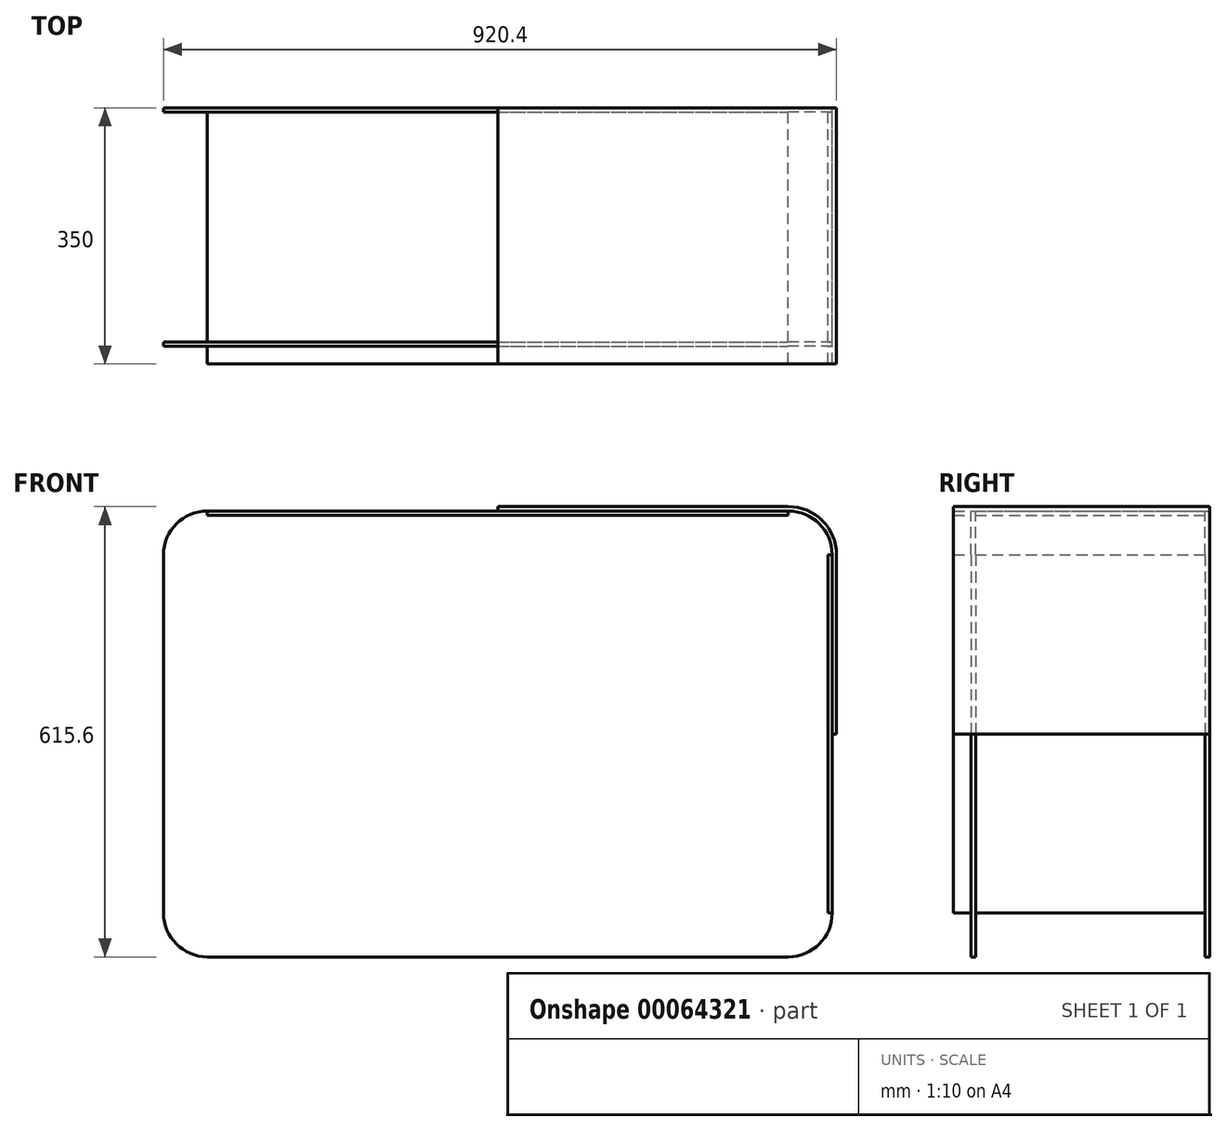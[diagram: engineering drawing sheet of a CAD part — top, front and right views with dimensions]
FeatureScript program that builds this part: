
annotation { "Feature Type Name" : "Feature", "Feature Type Description" : "" }
export const myFeature = defineFeature(function(context is Context, id is Id, definition is map)
    precondition{}
    {
        {
            var Q0;
            Q0=qCreatedBy(makeId("Front.planeOp"),FACE);
            var sketch = newSketch(context, id + "F0", { "sketchPlane" : qUnion([Q0])});
            skLineSegment(sketch, "E0.rect.bottom", {"start": v(397.2, 304.8) * mm, "end": v(0, 304.8) * mm});
            skLineSegment(sketch, "E0.rect.left", {"start": v(457.2, 244.8) * mm, "end": v(457.2, 0) * mm});
            skPoint(sketch, "E0.rect.middle", {"position": v(0, 0) * mm});
            skPoint(sketch, "E1.visualSharp", {"position": v(-457.2, 304.8) * mm});
            skPoint(sketch, "E2.visualSharp", {"position": v(457.2, 304.8) * mm});
            skArc(sketch, "E2.filletArc", {"start": v(457.2, 244.8) * mm, "mid": v(439.63, 287.23) * mm, "end": v(397.2, 304.8) * mm});
            skPoint(sketch, "E3.visualSharp", {"position": v(-457.2, -304.8) * mm});
            skPoint(sketch, "E4.visualSharp", {"position": v(457.2, -304.8) * mm});
            skLineSegment(sketch, "E5", {"start": v(0, 0) * mm, "end": v(0, 526.98) * mm});
            skLineSegment(sketch, "E6", {"start": v(667.96, 0) * mm, "end": v(0, 0) * mm});
            skLineSegment(sketch, "E7.0", {"start": v(397.2, 310.8) * mm, "end": v(0, 310.8) * mm});
            skArc(sketch, "E7.1", {"start": v(463.2, 244.8) * mm, "mid": v(443.87, 291.47) * mm, "end": v(397.2, 310.8) * mm});
            skLineSegment(sketch, "E7.2", {"start": v(463.2, 244.8) * mm, "end": v(463.2, 0) * mm});
            skLineSegment(sketch, "E8.0", {"start": v(397.2, 298.8) * mm, "end": v(0, 298.8) * mm});
            skLineSegment(sketch, "E9.0", {"start": v(451.2, 244.8) * mm, "end": v(451.2, 0) * mm});
            skLineSegment(sketch, "E10.MirrorCS", {"start": v(397.2, -304.8) * mm, "end": v(0, -304.8) * mm});
            skLineSegment(sketch, "E11.MirrorCS", {"start": v(457.2, -244.8) * mm, "end": v(457.2, 0) * mm});
            skLineSegment(sketch, "E12.MirrorCS", {"start": v(397.2, -310.8) * mm, "end": v(0, -310.8) * mm});
            skLineSegment(sketch, "E13.MirrorCS", {"start": v(451.2, -244.8) * mm, "end": v(451.2, 0) * mm});
            skArc(sketch, "E14.MirrorCS", {"start": v(457.2, -244.8) * mm, "mid": v(439.63, -287.23) * mm, "end": v(397.2, -304.8) * mm});
            skArc(sketch, "E15.MirrorCS", {"start": v(463.2, -244.8) * mm, "mid": v(443.87, -291.47) * mm, "end": v(397.2, -310.8) * mm});
            skLineSegment(sketch, "E16.MirrorCS", {"start": v(397.2, -298.8) * mm, "end": v(0, -298.8) * mm});
            skLineSegment(sketch, "E17.MirrorCS", {"start": v(463.2, -244.8) * mm, "end": v(463.2, 0) * mm});
            skLineSegment(sketch, "E18.bottom", {"start": v(1425.63, 785.2) * mm, "end": v(3864.03, 785.2) * mm});
            skLineSegment(sketch, "E18.top", {"start": v(1425.63, -434) * mm, "end": v(3864.03, -434) * mm});
            skLineSegment(sketch, "E18.left", {"start": v(1425.63, 785.2) * mm, "end": v(1425.63, -434) * mm});
            skLineSegment(sketch, "E18.right", {"start": v(3864.03, 785.2) * mm, "end": v(3864.03, -434) * mm});
            skLineSegment(sketch, "E19.bottom", {"start": v(1421.93, -434) * mm, "end": v(2621.93, -434) * mm});
            skLineSegment(sketch, "E19.top", {"start": v(1421.93, 366) * mm, "end": v(2621.93, 366) * mm});
            skLineSegment(sketch, "E19.left", {"start": v(1421.93, -434) * mm, "end": v(1421.93, 366) * mm});
            skLineSegment(sketch, "E19.right", {"start": v(2621.93, -434) * mm, "end": v(2621.93, 366) * mm});
            skLineSegment(sketch, "E20", {"start": v(2644.83, -434) * mm, "end": v(2644.83, 785.2) * mm});
            skArc(sketch, "E21.MirrorCS", {"start": v(-463.2, -244.8) * mm, "mid": v(-443.87, -291.47) * mm, "end": v(-397.2, -310.8) * mm});
            skArc(sketch, "E22.MirrorCS", {"start": v(-457.2, -244.8) * mm, "mid": v(-439.63, -287.23) * mm, "end": v(-397.2, -304.8) * mm});
            skLineSegment(sketch, "E23.MirrorCS", {"start": v(-397.2, 304.8) * mm, "end": v(0, 304.8) * mm});
            skLineSegment(sketch, "E24.MirrorCS", {"start": v(-397.2, -304.8) * mm, "end": v(0, -304.8) * mm});
            skArc(sketch, "E25.MirrorCS", {"start": v(-463.2, 244.8) * mm, "mid": v(-443.87, 291.47) * mm, "end": v(-397.2, 310.8) * mm});
            skArc(sketch, "E26.MirrorCS", {"start": v(-457.2, 244.8) * mm, "mid": v(-439.63, 287.23) * mm, "end": v(-397.2, 304.8) * mm});
            skLineSegment(sketch, "E27.MirrorCS", {"start": v(-457.2, 244.8) * mm, "end": v(-457.2, 0) * mm});
            skLineSegment(sketch, "E28.MirrorCS", {"start": v(-397.2, -298.8) * mm, "end": v(0, -298.8) * mm});
            skLineSegment(sketch, "E29.MirrorCS", {"start": v(-397.2, -310.8) * mm, "end": v(0, -310.8) * mm});
            skLineSegment(sketch, "E30.MirrorCS", {"start": v(-457.2, -244.8) * mm, "end": v(-457.2, 0) * mm});
            skLineSegment(sketch, "E31.MirrorCS", {"start": v(-451.2, 244.8) * mm, "end": v(-451.2, 0) * mm});
            skLineSegment(sketch, "E32.MirrorCS", {"start": v(-397.2, 298.8) * mm, "end": v(0, 298.8) * mm});
            skLineSegment(sketch, "E33.MirrorCS", {"start": v(-463.2, 244.8) * mm, "end": v(-463.2, 0) * mm});
            skLineSegment(sketch, "E34.MirrorCS", {"start": v(-463.2, -244.8) * mm, "end": v(-463.2, 0) * mm});
            skLineSegment(sketch, "E35.MirrorCS", {"start": v(-397.2, 310.8) * mm, "end": v(0, 310.8) * mm});
            skLineSegment(sketch, "E36.MirrorCS", {"start": v(-667.96, 0) * mm, "end": v(0, 0) * mm, "construction": true});
            skLineSegment(sketch, "E37.MirrorCS", {"start": v(-451.2, -244.8) * mm, "end": v(-451.2, 0) * mm});
            skLineSegment(sketch, "E38", {"start": v(397.2, 298.8) * mm, "end": v(397.2, 304.8) * mm});
            skLineSegment(sketch, "E39", {"start": v(451.2, 244.8) * mm, "end": v(457.2, 244.8) * mm});
            skLineSegment(sketch, "E40.MirrorCS", {"start": v(397.2, -298.8) * mm, "end": v(397.2, -304.8) * mm});
            skLineSegment(sketch, "E41.MirrorCS", {"start": v(451.2, -244.8) * mm, "end": v(457.2, -244.8) * mm});
            skLineSegment(sketch, "E42.MirrorCS", {"start": v(-397.2, 298.8) * mm, "end": v(-397.2, 304.8) * mm});
            skLineSegment(sketch, "E43.MirrorCS", {"start": v(-451.2, 244.8) * mm, "end": v(-457.2, 244.8) * mm});
            skLineSegment(sketch, "E44.MirrorCS", {"start": v(-451.2, -244.8) * mm, "end": v(-457.2, -244.8) * mm});
            skLineSegment(sketch, "E45.MirrorCS", {"start": v(-397.2, -298.8) * mm, "end": v(-397.2, -304.8) * mm});
            skLineSegment(sketch, "E46.bottom", {"start": v(1396.97, -1773.98) * mm, "end": v(1746.97, -1773.98) * mm});
            skLineSegment(sketch, "E46.top", {"start": v(1396.97, -2518.98) * mm, "end": v(1746.97, -2518.98) * mm});
            skLineSegment(sketch, "E46.left", {"start": v(1396.97, -1773.98) * mm, "end": v(1396.97, -2518.98) * mm});
            skLineSegment(sketch, "E46.right", {"start": v(1746.97, -1773.98) * mm, "end": v(1746.97, -2518.98) * mm});
            skLineSegment(sketch, "E47.1.0.0", {"start": v(1746.97, -2518.98) * mm, "end": v(2096.97, -2518.98) * mm});
            skLineSegment(sketch, "E47.1.0.1", {"start": v(2096.97, -1773.98) * mm, "end": v(2096.97, -2518.98) * mm});
            skLineSegment(sketch, "E47.1.0.2", {"start": v(1746.97, -1773.98) * mm, "end": v(2096.97, -1773.98) * mm});
            skLineSegment(sketch, "E47.2.0.0", {"start": v(2096.97, -2518.98) * mm, "end": v(2446.97, -2518.98) * mm});
            skLineSegment(sketch, "E47.2.0.1", {"start": v(2446.97, -1773.98) * mm, "end": v(2446.97, -2518.98) * mm});
            skLineSegment(sketch, "E47.2.0.2", {"start": v(2096.97, -1773.98) * mm, "end": v(2446.97, -1773.98) * mm});
            skLineSegment(sketch, "E47.direction1", {"start": v(1396.97, -2518.98) * mm, "end": v(1746.97, -2518.98) * mm, "construction": true});
            skLineSegment(sketch, "E48.bottom", {"start": v(2698.8, -1773.27) * mm, "end": v(3048.8, -1773.27) * mm});
            skLineSegment(sketch, "E48.top", {"start": v(2698.8, -2518.27) * mm, "end": v(3048.8, -2518.27) * mm});
            skLineSegment(sketch, "E48.left", {"start": v(2698.8, -1773.27) * mm, "end": v(2698.8, -2518.27) * mm});
            skLineSegment(sketch, "E48.right", {"start": v(3048.8, -1773.27) * mm, "end": v(3048.8, -2518.27) * mm});
            skLineSegment(sketch, "E49.bottom", {"start": v(1430.76, -3016.82) * mm, "end": v(2225.76, -3016.82) * mm});
            skLineSegment(sketch, "E49.top", {"start": v(1430.76, -3316.82) * mm, "end": v(2225.76, -3316.82) * mm});
            skLineSegment(sketch, "E49.left", {"start": v(1430.76, -3016.82) * mm, "end": v(1430.76, -3316.82) * mm});
            skLineSegment(sketch, "E49.right", {"start": v(2225.76, -3016.82) * mm, "end": v(2225.76, -3316.82) * mm});
            skLineSegment(sketch, "E50.bottom", {"start": v(4728.96, 341) * mm, "end": v(5643.36, 341) * mm});
            skLineSegment(sketch, "E50.top", {"start": v(4728.96, -268.6) * mm, "end": v(5643.36, -268.6) * mm});
            skLineSegment(sketch, "E50.left", {"start": v(4728.96, 341) * mm, "end": v(4728.96, -268.6) * mm});
            skLineSegment(sketch, "E50.right", {"start": v(5643.36, 341) * mm, "end": v(5643.36, -268.6) * mm});
            skLineSegment(sketch, "E51.bottom", {"start": v(3200.39, -380.36) * mm, "end": v(3809.99, -380.36) * mm});
            skLineSegment(sketch, "E51.top", {"start": v(3200.39, 534.04) * mm, "end": v(3809.99, 534.04) * mm});
            skLineSegment(sketch, "E51.left", {"start": v(3200.39, -380.36) * mm, "end": v(3200.39, 534.04) * mm});
            skLineSegment(sketch, "E51.right", {"start": v(3809.99, -380.36) * mm, "end": v(3809.99, 534.04) * mm});
            skLineSegment(sketch, "E52.bottom", {"start": v(3993.98, -1809.5) * mm, "end": v(6433.98, -1809.5) * mm});
            skLineSegment(sketch, "E52.top", {"start": v(3993.98, -3029.5) * mm, "end": v(6433.98, -3029.5) * mm});
            skLineSegment(sketch, "E52.left", {"start": v(3993.98, -1809.5) * mm, "end": v(3993.98, -3029.5) * mm});
            skLineSegment(sketch, "E52.right", {"start": v(6433.98, -1809.5) * mm, "end": v(6433.98, -3029.5) * mm});
            skLineSegment(sketch, "E53", {"start": v(5213.98, -1809.5) * mm, "end": v(5213.98, -3029.5) * mm});
            skLineSegment(sketch, "E54", {"start": v(3993.98, -2229.5) * mm, "end": v(5213.98, -2229.5) * mm});
            skLineSegment(sketch, "E55", {"start": v(5773.98, -1809.5) * mm, "end": v(5773.98, -3029.5) * mm});
            skSolve(sketch);
        }
        {
            var Q0;
            {var subQ1=sQuery(id+"F0.wireOp",EDGE,"E0.rect.bottom");Q0=makeQuery(id+"F0.imprint","IMPRINT",FACE,{"disambiguationData":[TD([[makeQuery(id+"F0.imprint","IMPRINT",EDGE,{"derivedFrom":subQ1}),-1.0]])]});}
            extrude(context, id + "F1", {"entities" : qUnion([Q0]), "depth" : 350 * mm});
        }
        {
            var Q0;
            {var subQ0=sQuery(id+"F0.wireOp",EDGE,"E23.MirrorCS");Q0=makeQuery(id+"F0.imprint","IMPRINT",FACE,{"disambiguationData":[TD([[makeQuery(id+"F0.imprint","IMPRINT",EDGE,{"derivedFrom":subQ0}),-1.0]])]});}
            var Q1;
            {var subQ0=sQuery(id+"F0.wireOp",EDGE,"E0.rect.bottom");Q1=makeQuery(id+"F0.imprint","IMPRINT",FACE,{"disambiguationData":[TD([[makeQuery(id+"F0.imprint","IMPRINT",EDGE,{"derivedFrom":subQ0}),1.0]])]});}
            var Q2;
            {var subQ0=sQuery(id+"F0.wireOp",EDGE,"E0.rect.left");Q2=makeQuery(id+"F0.imprint","IMPRINT",FACE,{"disambiguationData":[TD([[makeQuery(id+"F0.imprint","IMPRINT",EDGE,{"derivedFrom":subQ0}),-1.0]])]});}
            var Q3;
            {var subQ0=sQuery(id+"F0.wireOp",EDGE,"E11.MirrorCS");Q3=makeQuery(id+"F0.imprint","IMPRINT",FACE,{"disambiguationData":[TD([[makeQuery(id+"F0.imprint","IMPRINT",EDGE,{"derivedFrom":subQ0}),1.0]])]});}
            extrude(context, id + "F2", {"entities" : qUnion([Q0, Q1, Q2, Q3]), "depth" : 314 * mm});
        }
        {
            var Q0;
            Q0=makeQuery(id+"F2.opExtrude","SWEPT_BODY",BODY,{"disambiguationData":[OSD([sQuery(id+"F0.wireOp",EDGE,"E0.rect.bottom"),sQuery(id+"F0.wireOp",EDGE,"E8.0"),sQuery(id+"F0.wireOp",EDGE,"E23.MirrorCS"),sQuery(id+"F0.wireOp",EDGE,"E32.MirrorCS"),sQuery(id+"F0.wireOp",EDGE,"E38"),sQuery(id+"F0.wireOp",EDGE,"E42.MirrorCS")])]});
            var Q1;
            Q1=makeQuery(id+"F2.opExtrude","SWEPT_BODY",BODY,{"disambiguationData":[OSD([sQuery(id+"F0.wireOp",EDGE,"E0.rect.left"),sQuery(id+"F0.wireOp",EDGE,"E9.0"),sQuery(id+"F0.wireOp",EDGE,"E11.MirrorCS"),sQuery(id+"F0.wireOp",EDGE,"E13.MirrorCS"),sQuery(id+"F0.wireOp",EDGE,"E39"),sQuery(id+"F0.wireOp",EDGE,"E41.MirrorCS")])]});
            var Q2;
            Q2=makeQuery(id+"F2.opExtrude","SWEPT_EDGE",EDGE,{"disambiguationData":[OSD([sQuery(id+"F0.wireOp",EDGE,"E32.MirrorCS"),sQuery(id+"F0.wireOp",EDGE,"E42.MirrorCS")])]});
            transform(context, id + "F3", {"entities" : qUnion([Q0, Q1]), "transformType" : TransformType.TRANSLATION_DISTANCE, "transformDirection" : qUnion([Q2]), "distance" : 6 * mm, "oppositeDirection" : true, "makeCopy" : false});
        }
        {
            var Q0;
            {var subQ0=sQuery(id+"F0.wireOp",EDGE,"E0.rect.bottom");Q0=makeQuery(id+"F0.imprint","IMPRINT",FACE,{"disambiguationData":[TD([[makeQuery(id+"F0.imprint","IMPRINT",EDGE,{"derivedFrom":subQ0}),1.0]])]});}
            var Q1;
            {var subQ0=sQuery(id+"F0.wireOp",EDGE,"E0.rect.left");Q1=makeQuery(id+"F0.imprint","IMPRINT",FACE,{"disambiguationData":[TD([[makeQuery(id+"F0.imprint","IMPRINT",EDGE,{"derivedFrom":subQ0}),-1.0]])]});}
            var Q2;
            {var subQ0=sQuery(id+"F0.wireOp",EDGE,"E23.MirrorCS");Q2=makeQuery(id+"F0.imprint","IMPRINT",FACE,{"disambiguationData":[TD([[makeQuery(id+"F0.imprint","IMPRINT",EDGE,{"derivedFrom":subQ0}),-1.0]])]});}
            var Q3;
            {var subQ0=sQuery(id+"F0.wireOp",EDGE,"E11.MirrorCS");Q3=makeQuery(id+"F0.imprint","IMPRINT",FACE,{"disambiguationData":[TD([[makeQuery(id+"F0.imprint","IMPRINT",EDGE,{"derivedFrom":subQ0}),1.0]])]});}
            extrude(context, id + "F4", {"entities" : qUnion([Q0, Q1, Q2, Q3]), "depth" : 24 * mm});
        }
        {
            var Q0;
            Q0=makeQuery(id+"F4.opExtrude","SWEPT_BODY",BODY,{"disambiguationData":[OSD([sQuery(id+"F0.wireOp",EDGE,"E0.rect.left"),sQuery(id+"F0.wireOp",EDGE,"E9.0"),sQuery(id+"F0.wireOp",EDGE,"E11.MirrorCS"),sQuery(id+"F0.wireOp",EDGE,"E13.MirrorCS"),sQuery(id+"F0.wireOp",EDGE,"E39"),sQuery(id+"F0.wireOp",EDGE,"E41.MirrorCS")])]});
            var Q1;
            Q1=makeQuery(id+"F4.opExtrude","SWEPT_BODY",BODY,{"disambiguationData":[OSD([sQuery(id+"F0.wireOp",EDGE,"E0.rect.bottom"),sQuery(id+"F0.wireOp",EDGE,"E8.0"),sQuery(id+"F0.wireOp",EDGE,"E23.MirrorCS"),sQuery(id+"F0.wireOp",EDGE,"E32.MirrorCS"),sQuery(id+"F0.wireOp",EDGE,"E38"),sQuery(id+"F0.wireOp",EDGE,"E42.MirrorCS")])]});
            var Q2;
            Q2=makeQuery(id+"F2.opExtrude","SWEPT_EDGE",EDGE,{"disambiguationData":[OSD([sQuery(id+"F0.wireOp",EDGE,"E8.0"),sQuery(id+"F0.wireOp",EDGE,"E38")])]});
            transform(context, id + "F5", {"entities" : qUnion([Q0, Q1]), "transformType" : TransformType.TRANSLATION_DISTANCE, "transformDirection" : qUnion([Q2]), "distance" : 326 * mm, "oppositeDirection" : true, "makeCopy" : false});
        }
        {
            var Q0;
            {var subQ0=sQuery(id+"F0.wireOp",EDGE,"E0.rect.left");Q0=makeQuery(id+"F0.imprint","IMPRINT",FACE,{"disambiguationData":[TD([[makeQuery(id+"F0.imprint","IMPRINT",EDGE,{"derivedFrom":subQ0}),-1.0]])]});}
            var Q1;
            Q1=makeQuery(id+"F0.imprint","IMPRINT",FACE,{"disambiguationData":[TD([[makeQuery(id+"F0.imprint","IMPRINT",EDGE,{"derivedFrom":sQuery(id+"F0.wireOp",EDGE,"E2.filletArc")}),1.0]])]});
            var Q2;
            {var subQ0=sQuery(id+"F0.wireOp",EDGE,"E11.MirrorCS");Q2=makeQuery(id+"F0.imprint","IMPRINT",FACE,{"disambiguationData":[TD([[makeQuery(id+"F0.imprint","IMPRINT",EDGE,{"derivedFrom":subQ0}),1.0]])]});}
            var Q3;
            {var subQ4=sQuery(id+"F0.wireOp",EDGE,"E13.MirrorCS");Q3=makeQuery(id+"F0.imprint","IMPRINT",FACE,{"disambiguationData":[TD([[makeQuery(id+"F0.imprint","IMPRINT",EDGE,{"derivedFrom":subQ4}),1.0]])]});}
            var Q4;
            Q4=makeQuery(id+"F0.imprint","IMPRINT",FACE,{"disambiguationData":[TD([[makeQuery(id+"F0.imprint","IMPRINT",EDGE,{"derivedFrom":sQuery(id+"F0.wireOp",EDGE,"E27.MirrorCS")}),1.0]])]});
            var Q5;
            Q5=makeQuery(id+"F0.imprint","IMPRINT",FACE,{"disambiguationData":[TD([[makeQuery(id+"F0.imprint","IMPRINT",EDGE,{"derivedFrom":sQuery(id+"F0.wireOp",EDGE,"E10.MirrorCS")}),-1.0]])]});
            var Q6;
            {var subQ0=sQuery(id+"F0.wireOp",EDGE,"E23.MirrorCS");Q6=makeQuery(id+"F0.imprint","IMPRINT",FACE,{"disambiguationData":[TD([[makeQuery(id+"F0.imprint","IMPRINT",EDGE,{"derivedFrom":subQ0}),-1.0]])]});}
            var Q7;
            {var subQ0=sQuery(id+"F0.wireOp",EDGE,"E0.rect.bottom");Q7=makeQuery(id+"F0.imprint","IMPRINT",FACE,{"disambiguationData":[TD([[makeQuery(id+"F0.imprint","IMPRINT",EDGE,{"derivedFrom":subQ0}),1.0]])]});}
            extrude(context, id + "F6", {"entities" : qUnion([Q0, Q1, Q2, Q3, Q4, Q5, Q6, Q7]), "depth" : 6 * mm});
        }
        {
            var Q0;
            Q0=makeQuery(id+"F6.opExtrude","SWEPT_BODY",BODY,{"disambiguationData":[OSD([sQuery(id+"F0.wireOp",EDGE,"E0.rect.bottom"),sQuery(id+"F0.wireOp",EDGE,"E0.rect.left"),sQuery(id+"F0.wireOp",EDGE,"E2.filletArc"),sQuery(id+"F0.wireOp",EDGE,"E10.MirrorCS"),sQuery(id+"F0.wireOp",EDGE,"E11.MirrorCS"),sQuery(id+"F0.wireOp",EDGE,"E14.MirrorCS"),sQuery(id+"F0.wireOp",EDGE,"E22.MirrorCS"),sQuery(id+"F0.wireOp",EDGE,"E23.MirrorCS"),sQuery(id+"F0.wireOp",EDGE,"E24.MirrorCS"),sQuery(id+"F0.wireOp",EDGE,"E26.MirrorCS"),sQuery(id+"F0.wireOp",EDGE,"E27.MirrorCS"),sQuery(id+"F0.wireOp",EDGE,"E30.MirrorCS")])]});
            var Q1;
            Q1=makeQuery(id+"F2.opExtrude","SWEPT_EDGE",EDGE,{"disambiguationData":[OSD([sQuery(id+"F0.wireOp",EDGE,"E13.MirrorCS"),sQuery(id+"F0.wireOp",EDGE,"E41.MirrorCS")])]});
            var Q2;
            Q2=makeQuery(id+"F2.opExtrude","SWEPT_EDGE",EDGE,{"disambiguationData":[OSD([sQuery(id+"F0.wireOp",EDGE,"E11.MirrorCS"),sQuery(id+"F0.wireOp",EDGE,"E14.MirrorCS"),sQuery(id+"F0.wireOp",EDGE,"E41.MirrorCS")])]});
            transform(context, id + "F7", {"entities" : qUnion([Q0]), "transformType" : TransformType.TRANSLATION_DISTANCE, "transformDirection" : qUnion([Q2]), "distance" : 320 * mm, "oppositeDirection" : true, "makeCopy" : true});
        }
    });
